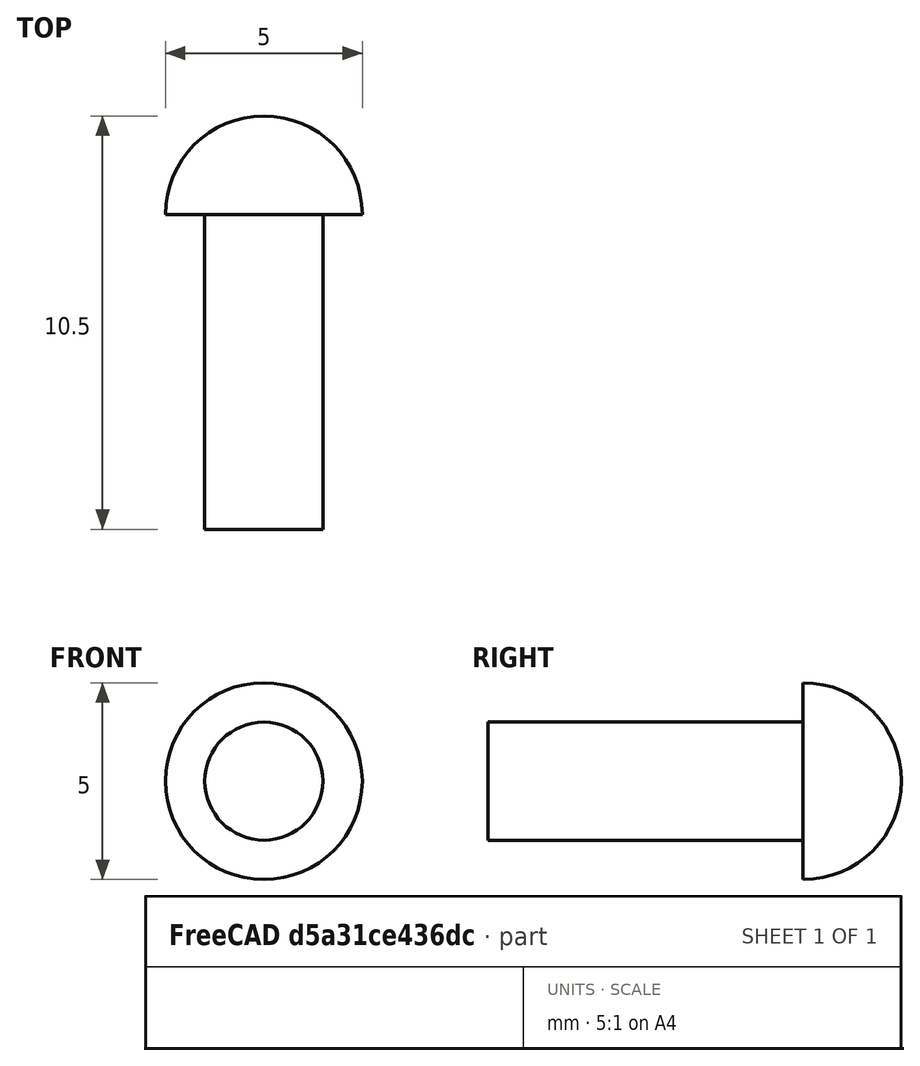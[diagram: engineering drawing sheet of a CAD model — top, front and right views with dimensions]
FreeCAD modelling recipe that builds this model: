
FCSTD DOCUMENT  (FreeCAD 0.19R)
Label: Rivet_8
License: All rights reserved
LicenseURL: http://en.wikipedia.org/wiki/All_rights_reserved
objects: Sketcher::SketchObject×1, PartDesign::Revolution×1, PartDesign::Body×1
note: 4 computed .brp shape members not serialized (recipe doc carries the construction recipe); baked Part::Feature solids carry a one-line shape summary decoded from their .brp

FEATURE [Sketcher::SketchObject] Sketch
  FullyConstrained = true
  MapMode = 5
  Support = -> [XY_Plane]
  sketch-geometry (5):
    g0: LineSegment StartX=0 StartY=0 StartZ=0 EndX=1.5 EndY=0 EndZ=0
    g1: LineSegment StartX=1.5 StartY=0 StartZ=0 EndX=1.5 EndY=8 EndZ=0
    g2: ArcOfCircle CenterX=0 CenterY=8 CenterZ=0 NormalX=0 NormalY=0 NormalZ=1 AngleXU=0 Radius=2.5 StartAngle=0 EndAngle=1.5708
    g3: LineSegment StartX=2e-16 StartY=10.5 StartZ=0 EndX=0 EndY=0 EndZ=0
    g4: LineSegment StartX=1.5 StartY=8 StartZ=0 EndX=2.5 EndY=8 EndZ=0
  constraints (15):
    c: Coincident(g0,g-1)
    c: PointOnObject(g0,g-1)
    c: DistanceX(g0,g0) = 1.5
    c: Coincident(g1,g0)
    c: Vertical(g1)
    c: DistanceY(g1,g1) = 8
    c: PointOnObject(g2,g-2)
    c: PointOnObject(g2,g-2)
    c: Horizontal(g1,g2)
    c: Diameter(g2) = 5
    c: Coincident(g3,g2)
    c: Coincident(g3,g0)
    c: Coincident(g4,g1)
    c: Coincident(g4,g2)
    c: Horizontal(g4)
FEATURE [PartDesign::Revolution] Revolution
  Angle = 360
  Axis = (0,1,0)
  Base = (0,0,0)
  Profile = -> Sketch
  ReferenceAxis = -> Sketch [V_Axis]
  Reversed = true
FEATURE [PartDesign::Body] Body
  Group = -> [Sketch,Revolution]
  Origin = -> Origin
  Tip = -> Revolution
